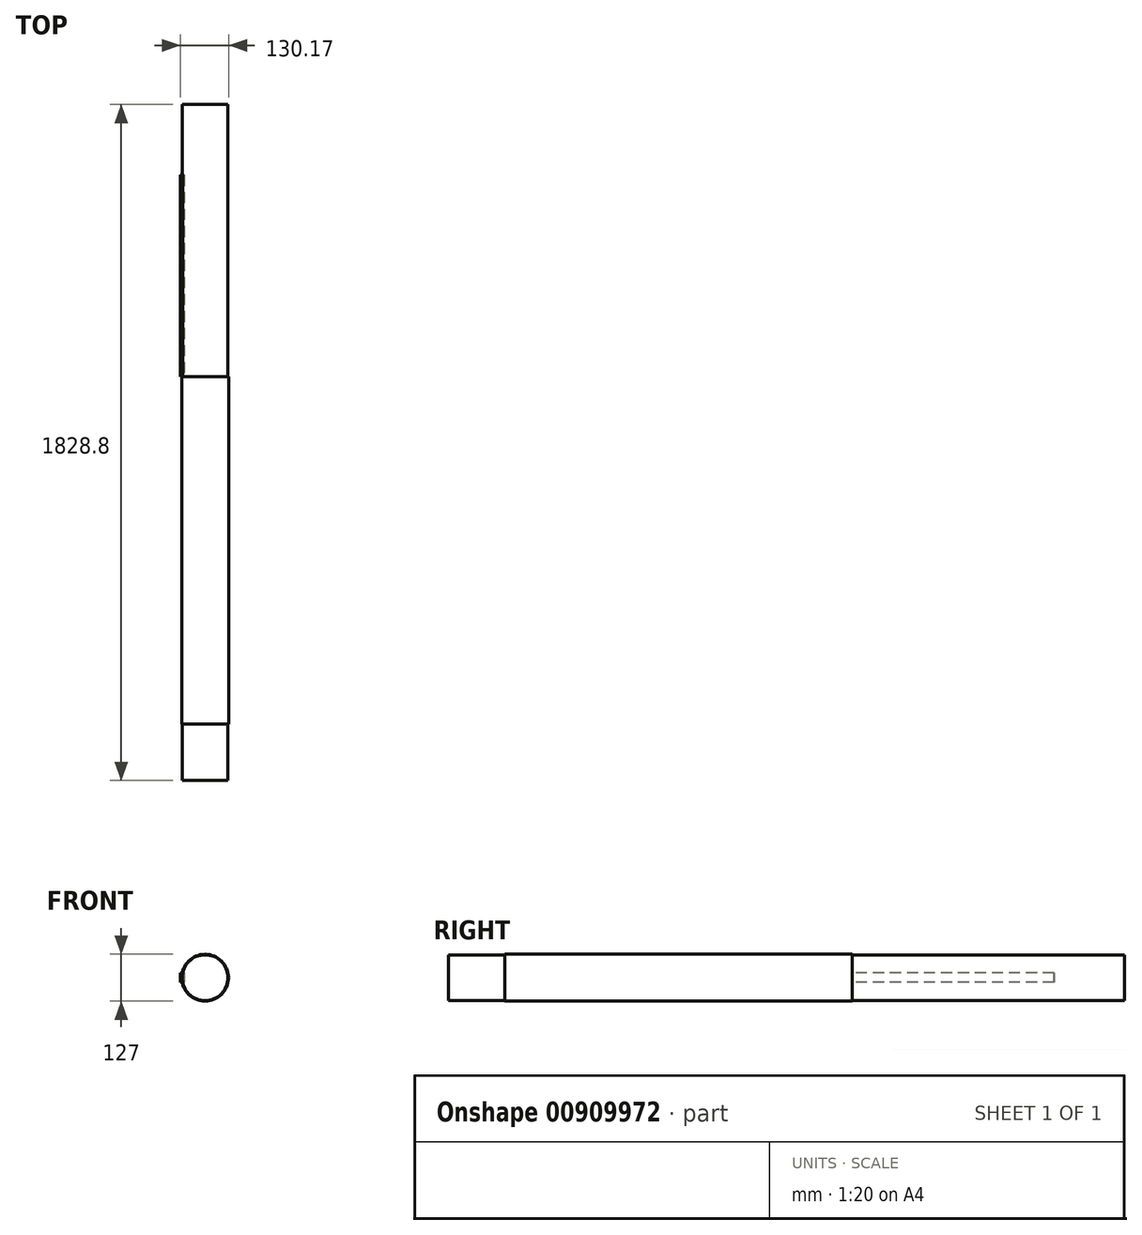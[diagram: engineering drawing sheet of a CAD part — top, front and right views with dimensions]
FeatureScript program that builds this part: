
annotation { "Feature Type Name" : "Feature", "Feature Type Description" : "" }
export const myFeature = defineFeature(function(context is Context, id is Id, definition is map)
    precondition{}
    {
        {
            var Q0;
            Q0=qCreatedBy(makeId("Right.planeOp"),FACE);
            var sketch = newSketch(context, id + "F0", { "sketchPlane" : qUnion([Q0])});
            skLineSegment(sketch, "E0.bottom", {"start": v(0, 0) * mm, "end": v(-1828.8, 0) * mm});
            skLineSegment(sketch, "E0.top", {"start": v(0, 61.91) * mm, "end": v(-736.6, 61.91) * mm});
            skLineSegment(sketch, "E0.left", {"start": v(0, 0) * mm, "end": v(0, 61.91) * mm});
            skLineSegment(sketch, "E0.right", {"start": v(-1828.8, 0) * mm, "end": v(-1828.8, 61.91) * mm});
            skLineSegment(sketch, "E1", {"start": v(0, 0) * mm, "end": v(27.92, 0) * mm, "construction": true});
            skLineSegment(sketch, "E2.top", {"start": v(-1676.4, 63.5) * mm, "end": v(-736.6, 63.5) * mm});
            skLineSegment(sketch, "E2.left", {"start": v(-1676.4, 61.91) * mm, "end": v(-1676.4, 63.5) * mm});
            skLineSegment(sketch, "E2.right", {"start": v(-736.6, 61.91) * mm, "end": v(-736.6, 63.5) * mm});
            skLineSegment(sketch, "E3.trimOffspring", {"start": v(-1676.4, 61.91) * mm, "end": v(-1828.8, 61.91) * mm});
            skSolve(sketch);
        }
        {
            var Q0;
            Q0=makeQuery(id+"F0.imprint","IMPRINT",FACE,{"disambiguationData":[TD([[makeQuery(id+"F0.imprint","IMPRINT",EDGE,{"derivedFrom":sQuery(id+"F0.wireOp",EDGE,"E0.bottom")}),-1.0]])]});
            var Q1;
            Q1=sQuery(id+"F0.wireOp",EDGE,"E1");
            revolve(context, id + "F1", {"surfaceOperationType" : NewSurfaceOperationType.NEW, "entities" : qUnion([Q0]), "axis" : qUnion([Q1]), "revolveType" : RevolveType.FULL});
        }
        {
            var Q0;
            Q0=makeQuery(id+"F1.opRevolve","SWEPT_FACE",FACE,{"disambiguationData":[OSD([sQuery(id+"F0.wireOp",EDGE,"E2.right")])]});
            var sketch = newSketch(context, id + "F2", { "sketchPlane" : qUnion([Q0])});
            skLineSegment(sketch, "E4.bottom", {"start": v(57.15, 12.7) * mm, "end": v(66.67, 12.7) * mm});
            skLineSegment(sketch, "E4.top", {"start": v(57.15, -12.7) * mm, "end": v(66.67, -12.7) * mm});
            skLineSegment(sketch, "E4.left", {"start": v(57.15, 12.7) * mm, "end": v(57.15, -12.7) * mm});
            skLineSegment(sketch, "E4.right", {"start": v(66.67, 12.7) * mm, "end": v(66.67, -12.7) * mm});
            skLineSegment(sketch, "E5", {"start": v(66.67, 0) * mm, "end": v(0, 0) * mm, "construction": true});
            skSolve(sketch);
        }
        {
            var Q0;
            {var subQ0=sQuery(id+"F2.wireOp",EDGE,"E4.top");Q0=makeQuery(id+"F2.imprint","IMPRINT",FACE,{"disambiguationData":[TD([[makeQuery(id+"F2.imprint","IMPRINT",EDGE,{"derivedFrom":subQ0}),1.0]])]});}
            extrude(context, id + "F3", {"entities" : qUnion([Q0]), "operationType" : NewBodyOperationType.REMOVE, "depth" : 546.1 * mm, "offsetDistance" : 25 * mm});
        }
        {
            var Q0;
            {var subQ0=sQuery(id+"F2.wireOp",EDGE,"E4.right");Q0=makeQuery(id+"F2.imprint","IMPRINT",FACE,{"disambiguationData":[TD([[makeQuery(id+"F2.imprint","IMPRINT",EDGE,{"derivedFrom":subQ0}),-1.0]])]});}
            var Q1;
            {var subQ0=sQuery(id+"F2.wireOp",EDGE,"E4.left");Q1=makeQuery(id+"F2.imprint","IMPRINT",FACE,{"disambiguationData":[TD([[makeQuery(id+"F2.imprint","IMPRINT",EDGE,{"derivedFrom":subQ0}),1.0]])]});}
            var Q2;
            {var subQ0=sQuery(id+"F2.wireOp",EDGE,"E4.bottom");var subQ1=sQuery(id+"F0.wireOp",EDGE,"E2.right");var subQ2=makeQuery(id+"F1.opRevolve","SWEPT_EDGE",EDGE,{"disambiguationData":[OSD([sQuery(id+"F0.wireOp",EDGE,"E2.top"),subQ1])]});var subQ3=makeQuery(id+"F2.imprint","INTERSECT",VERTEX,{"derivedFrom":[subQ2,subQ0]});Q2=makeQuery(id+"F2.imprint","IMPRINT",FACE,{"disambiguationData":[TD([[makeQuery(id+"F2.imprint","IMPRINT",EDGE,{"disambiguationData":[TD([[subQ3,1.0]])],"derivedFrom":subQ0}),-1.0]])]});}
            extrude(context, id + "F4", {"entities" : qUnion([Q0, Q1, Q2]), "depth" : 546.1 * mm, "offsetDistance" : 25 * mm});
        }
    });
